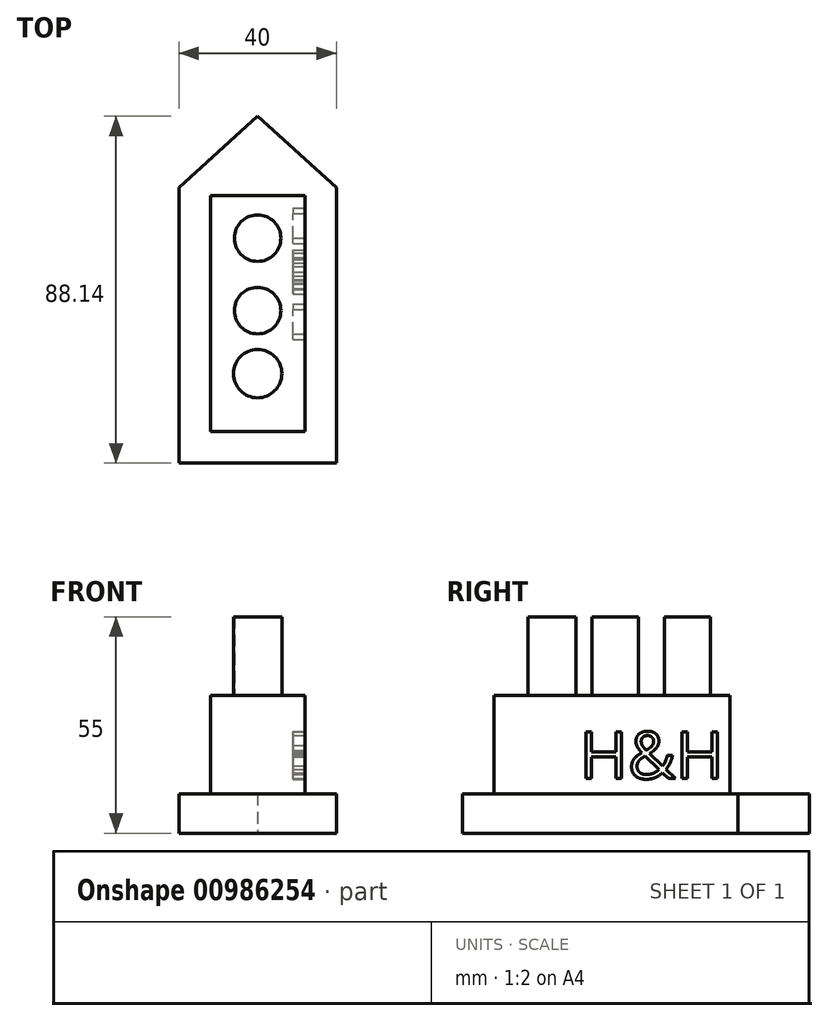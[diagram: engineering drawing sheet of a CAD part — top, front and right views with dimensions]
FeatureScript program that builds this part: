
annotation { "Feature Type Name" : "Feature", "Feature Type Description" : "" }
export const myFeature = defineFeature(function(context is Context, id is Id, definition is map)
    precondition{}
    {
        {
            var Q0;
            Q0=qCreatedBy(makeId("Top.planeOp"),FACE);
            var sketch = newSketch(context, id + "F0", { "sketchPlane" : qUnion([Q0])});
            skLineSegment(sketch, "E0", {"start": v(-20, 47.23) * mm, "end": v(-20, -22.77) * mm});
            skLineSegment(sketch, "E1", {"start": v(-20, -22.77) * mm, "end": v(20, -22.77) * mm});
            skLineSegment(sketch, "E2", {"start": v(20, -22.77) * mm, "end": v(20, 47.23) * mm});
            skLineSegment(sketch, "E3", {"start": v(0, 65.37) * mm, "end": v(20, 47.23) * mm});
            skLineSegment(sketch, "E4", {"start": v(0, 65.37) * mm, "end": v(-20, 47.23) * mm});
            skSolve(sketch);
        }
        {
            var Q0;
            Q0=makeQuery(id+"F0.imprint","IMPRINT",FACE,{"disambiguationData":[TD([[makeQuery(id+"F0.imprint","IMPRINT",EDGE,{"derivedFrom":sQuery(id+"F0.wireOp",EDGE,"E0")}),1.0]])]});
            extrude(context, id + "F1", {"entities" : qUnion([Q0]), "depth" : 10 * mm, "offsetDistance" : 25 * mm});
        }
        {
            var Q0;
            Q0=makeQuery(id+"F1.opExtrude","CAP_FACE",FACE,{"disambiguationData":[OSD([sQuery(id+"F0.wireOp",EDGE,"E0"),sQuery(id+"F0.wireOp",EDGE,"E1"),sQuery(id+"F0.wireOp",EDGE,"E2"),sQuery(id+"F0.wireOp",EDGE,"E3"),sQuery(id+"F0.wireOp",EDGE,"E4")])],"isStart":false});
            var sketch = newSketch(context, id + "F2", { "sketchPlane" : qUnion([Q0])});
            skLineSegment(sketch, "E5.bottom", {"start": v(-12, 45.23) * mm, "end": v(12, 45.23) * mm});
            skLineSegment(sketch, "E5.top", {"start": v(-12, -14.77) * mm, "end": v(12, -14.77) * mm});
            skLineSegment(sketch, "E5.left", {"start": v(-12, 45.23) * mm, "end": v(-12, -14.77) * mm});
            skLineSegment(sketch, "E5.right", {"start": v(12, 45.23) * mm, "end": v(12, -14.77) * mm});
            skSolve(sketch);
        }
        {
            var Q0;
            Q0 = qSketchRegion(id + "F2", true);
            extrude(context, id + "F3", {"entities" : qUnion([Q0]), "operationType" : NewBodyOperationType.ADD, "depth" : 25 * mm, "offsetDistance" : 25 * mm});
        }
        {
            var Q0;
            Q0=makeQuery(id+"F3.opExtrude","CAP_FACE",FACE,{"disambiguationData":[OSD([sQuery(id+"F2.wireOp",EDGE,"E5.bottom"),sQuery(id+"F2.wireOp",EDGE,"E5.top"),sQuery(id+"F2.wireOp",EDGE,"E5.left"),sQuery(id+"F2.wireOp",EDGE,"E5.right")])],"isStart":false});
            var sketch = newSketch(context, id + "F4", { "sketchPlane" : qUnion([Q0])});
            skSolve(sketch);
        }
        {
            var Q0;
            Q0=makeQuery(id+"F4.imprint","IMPRINT",FACE,{"disambiguationData":[TD([[makeQuery(id+"F4.imprint","IMPRINT",EDGE,{"derivedFrom":makeQuery(id+"F3.opExtrude","CAP_EDGE",EDGE,{"disambiguationData":[OSD([sQuery(id+"F2.wireOp",EDGE,"E5.bottom")])],"isStart":false})}),-1.0]])]});
            var sketch = newSketch(context, id + "F5", { "sketchPlane" : qUnion([Q0])});
            skCircle(sketch, "E6", {"center": v(0, 34.42) * mm, "radius": 5.9 * mm});
            skCircle(sketch, "E7", {"center": v(0, 16) * mm, "radius": 5.9 * mm});
            skCircle(sketch, "E8", {"center": v(0, 0) * mm, "radius": 6.14 * mm});
            skSolve(sketch);
        }
        {
            var Q0;
            Q0=makeQuery(id+"F5.imprint","IMPRINT",FACE,{"disambiguationData":[TD([[makeQuery(id+"F5.imprint","IMPRINT",EDGE,{"derivedFrom":sQuery(id+"F5.wireOp",EDGE,"E6")}),1.0]])]});
            var Q1;
            Q1=makeQuery(id+"F5.imprint","IMPRINT",FACE,{"disambiguationData":[TD([[makeQuery(id+"F5.imprint","IMPRINT",EDGE,{"derivedFrom":sQuery(id+"F5.wireOp",EDGE,"E8")}),1.0]])]});
            var Q2;
            Q2=makeQuery(id+"F5.imprint","IMPRINT",FACE,{"disambiguationData":[TD([[makeQuery(id+"F5.imprint","IMPRINT",EDGE,{"derivedFrom":sQuery(id+"F5.wireOp",EDGE,"E7")}),1.0]])]});
            extrude(context, id + "F6", {"entities" : qUnion([Q0, Q1, Q2]), "operationType" : NewBodyOperationType.ADD, "depth" : 20 * mm, "offsetDistance" : 25 * mm});
        }
        {
            var Q0;
            Q0=makeQuery(id+"F3.opExtrude","SWEPT_FACE",FACE,{"disambiguationData":[OSD([sQuery(id+"F2.wireOp",EDGE,"E5.right")])]});
            var sketch = newSketch(context, id + "F7", { "sketchPlane" : qUnion([Q0])});
            skSolve(sketch);
        }
        {
            var Q0;
            {var subQ0=sQuery(id+"F2.wireOp",EDGE,"E5.right");Q0=makeQuery(id+"F7.imprint","IMPRINT",FACE,{"disambiguationData":[TD([[makeQuery(id+"F7.imprint","IMPRINT",EDGE,{"derivedFrom":makeQuery(id+"F3.opExtrude","CAP_EDGE",EDGE,{"disambiguationData":[OSD([subQ0])],"isStart":false})}),1.0]])]});}
            var sketch = newSketch(context, id + "F8", { "sketchPlane" : qUnion([Q0])});
            skText(sketch, "E9", { "text": "H&H", "fontName": "OpenSans-Regular.ttf"});
            const initialGuessF8  = {"E9": [0.00705, 0.01386, 1, 0, 0.01196]};
            skSetInitialGuess(sketch, initialGuessF8);
            skSolve(sketch);
        }
        {
            var Q0;
            Q0 = qSketchRegion(id + "F8", true);
            extrude(context, id + "F9", {"entities" : qUnion([Q0]), "operationType" : NewBodyOperationType.REMOVE, "oppositeDirection" : true, "depth" : 3 * mm, "offsetDistance" : 25 * mm});
        }
    });
